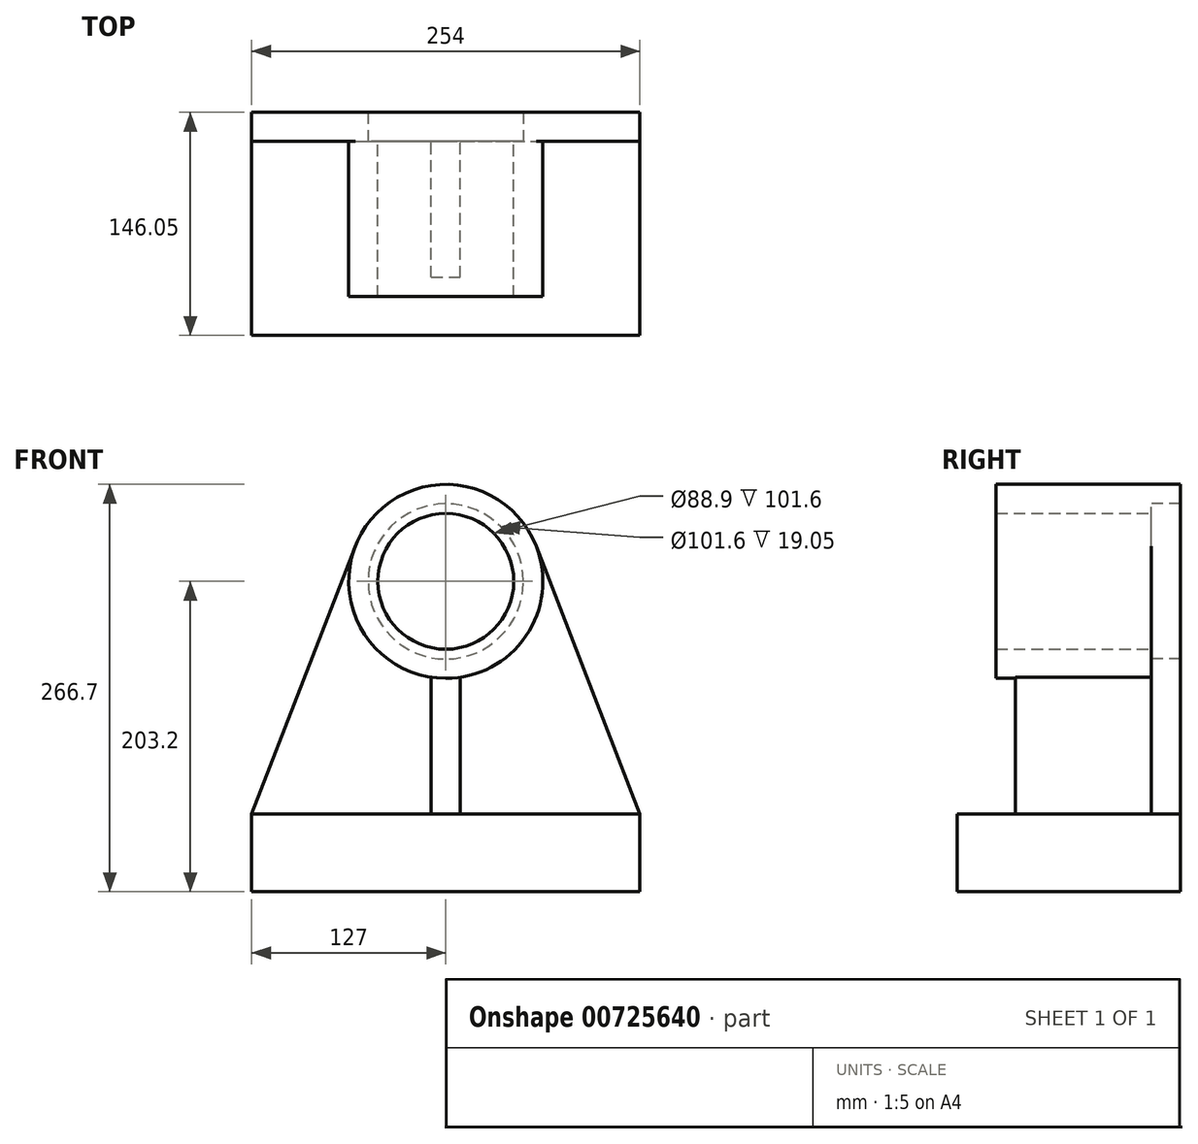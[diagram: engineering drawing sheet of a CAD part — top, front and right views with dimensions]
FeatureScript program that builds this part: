
annotation { "Feature Type Name" : "Feature", "Feature Type Description" : "" }
export const myFeature = defineFeature(function(context is Context, id is Id, definition is map)
    precondition{}
    {
        {
            var Q0;
            Q0=qCreatedBy(makeId("Front.planeOp"),FACE);
            var sketch = newSketch(context, id + "F0", { "sketchPlane" : qUnion([Q0])});
            skLineSegment(sketch, "E0", {"start": v(0, 0) * mm, "end": v(254, 0) * mm});
            skLineSegment(sketch, "E1", {"start": v(254, 0) * mm, "end": v(254, 50.8) * mm});
            skLineSegment(sketch, "E2", {"start": v(254, 50.8) * mm, "end": v(186.23, 226.1) * mm});
            skLineSegment(sketch, "E3", {"start": v(0, 0) * mm, "end": v(0, 50.8) * mm});
            skLineSegment(sketch, "E4", {"start": v(0, 50.8) * mm, "end": v(67.77, 226.1) * mm});
            skArc(sketch, "E5", {"start": v(186.23, 226.1) * mm, "mid": v(127, 266.7) * mm, "end": v(67.77, 226.1) * mm});
            skSolve(sketch);
        }
        {
            var Q0;
            Q0=makeQuery(id+"F0.imprint","IMPRINT",FACE,{"disambiguationData":[TD([[makeQuery(id+"F0.imprint","IMPRINT",EDGE,{"derivedFrom":sQuery(id+"F0.wireOp",EDGE,"E0")}),1.0]])]});
            extrude(context, id + "F1", {"entities" : qUnion([Q0]), "depth" : 19.05 * mm, "offsetDistance" : 25.4 * mm});
        }
        {
            var Q0;
            Q0=makeQuery(id+"F1.opExtrude","CAP_FACE",FACE,{"disambiguationData":[OSD([sQuery(id+"F0.wireOp",EDGE,"E0"),sQuery(id+"F0.wireOp",EDGE,"E1"),sQuery(id+"F0.wireOp",EDGE,"E2"),sQuery(id+"F0.wireOp",EDGE,"E3"),sQuery(id+"F0.wireOp",EDGE,"E4"),sQuery(id+"F0.wireOp",EDGE,"E5")])],"isStart":false});
            var sketch = newSketch(context, id + "F2", { "sketchPlane" : qUnion([Q0])});
            skCircle(sketch, "E6", {"center": v(127, 203.2) * mm, "radius": 44.45 * mm});
            skCircle(sketch, "E7", {"center": v(127, 203.2) * mm, "radius": 63.5 * mm});
            skSolve(sketch);
        }
        {
            var Q0;
            Q0=makeQuery(id+"F2.imprint","IMPRINT",FACE,{"disambiguationData":[TD([[makeQuery(id+"F2.imprint","IMPRINT",EDGE,{"derivedFrom":sQuery(id+"F2.wireOp",EDGE,"E6")}),-1.0]])]});
            extrude(context, id + "F3", {"entities" : qUnion([Q0]), "operationType" : NewBodyOperationType.ADD, "depth" : 101.6 * mm, "offsetDistance" : 25.4 * mm});
        }
        {
            var Q0;
            {var subQ0=sQuery(id+"F0.wireOp",EDGE,"E2");var subQ1=sQuery(id+"F0.wireOp",EDGE,"E1");var subQ2=sQuery(id+"F0.wireOp",EDGE,"E3");var subQ3=sQuery(id+"F0.wireOp",EDGE,"E0");var subQ4=sQuery(id+"F0.wireOp",EDGE,"E4");var subQ5=sQuery(id+"F0.wireOp",EDGE,"E5");Q0=makeQuery(id+"F3.boolean.opBoolean","SPLIT",FACE,{"disambiguationData":[TD([makeQuery(id+"F1.opExtrude","SWEPT_FACE",FACE,{"disambiguationData":[OSD([subQ3])]})])],"derivedFrom":makeQuery(id+"F1.opExtrude","CAP_FACE",FACE,{"disambiguationData":[OSD([subQ3,subQ1,subQ0,subQ2,subQ4,subQ5])],"isStart":false})});}
            var sketch = newSketch(context, id + "F4", { "sketchPlane" : qUnion([Q0])});
            skLineSegment(sketch, "E8.bottom", {"start": v(0, 0) * mm, "end": v(254, 0) * mm});
            skLineSegment(sketch, "E8.top", {"start": v(0, 50.8) * mm, "end": v(254, 50.8) * mm});
            skLineSegment(sketch, "E8.left", {"start": v(0, 0) * mm, "end": v(0, 50.8) * mm});
            skLineSegment(sketch, "E8.right", {"start": v(254, 0) * mm, "end": v(254, 50.8) * mm});
            skSolve(sketch);
        }
        {
            var Q0;
            Q0 = qSketchRegion(id + "F4", true);
            extrude(context, id + "F5", {"entities" : qUnion([Q0]), "operationType" : NewBodyOperationType.ADD, "depth" : 127 * mm, "offsetDistance" : 25.4 * mm});
        }
        {
            var Q0;
            {var subQ0=sQuery(id+"F0.wireOp",EDGE,"E2");var subQ1=sQuery(id+"F0.wireOp",EDGE,"E1");var subQ2=sQuery(id+"F0.wireOp",EDGE,"E3");var subQ3=sQuery(id+"F0.wireOp",EDGE,"E0");var subQ4=sQuery(id+"F0.wireOp",EDGE,"E4");var subQ5=sQuery(id+"F0.wireOp",EDGE,"E5");Q0=makeQuery(id+"F3.boolean.opBoolean","SPLIT",FACE,{"disambiguationData":[TD([makeQuery(id+"F1.opExtrude","SWEPT_FACE",FACE,{"disambiguationData":[OSD([subQ3])]})])],"derivedFrom":makeQuery(id+"F1.opExtrude","CAP_FACE",FACE,{"disambiguationData":[OSD([subQ3,subQ1,subQ0,subQ2,subQ4,subQ5])],"isStart":false})});}
            var sketch = newSketch(context, id + "F6", { "sketchPlane" : qUnion([Q0])});
            skLineSegment(sketch, "E9", {"start": v(117.48, 50.8) * mm, "end": v(136.53, 50.8) * mm});
            skLineSegment(sketch, "E10", {"start": v(136.53, 50.8) * mm, "end": v(136.53, 140.42) * mm});
            skLineSegment(sketch, "E11", {"start": v(117.48, 50.8) * mm, "end": v(117.48, 140.42) * mm});
            skArc(sketch, "E12", {"start": v(117.48, 140.42) * mm, "mid": v(127, 139.82) * mm, "end": v(136.53, 140.42) * mm});
            skSolve(sketch);
        }
        {
            var Q0;
            Q0 = qSketchRegion(id + "F6", true);
            extrude(context, id + "F7", {"entities" : qUnion([Q0]), "operationType" : NewBodyOperationType.ADD, "depth" : 88.9 * mm, "offsetDistance" : 25.4 * mm});
        }
        {
            var Q0;
            Q0=makeQuery(id+"F3.boolean.opBoolean","SPLIT",FACE,{"disambiguationData":[TD([makeQuery(id+"F3.opExtrude","SWEPT_FACE",FACE,{"disambiguationData":[OSD([sQuery(id+"F2.wireOp",EDGE,"E6")])]})])],"derivedFrom":makeQuery(id+"F1.opExtrude","CAP_FACE",FACE,{"disambiguationData":[OSD([sQuery(id+"F0.wireOp",EDGE,"E0"),sQuery(id+"F0.wireOp",EDGE,"E1"),sQuery(id+"F0.wireOp",EDGE,"E2"),sQuery(id+"F0.wireOp",EDGE,"E3"),sQuery(id+"F0.wireOp",EDGE,"E4"),sQuery(id+"F0.wireOp",EDGE,"E5")])],"isStart":false})});
            var sketch = newSketch(context, id + "F8", { "sketchPlane" : qUnion([Q0])});
            skCircle(sketch, "E13", {"center": v(127, 203.2) * mm, "radius": 50.8 * mm});
            skSolve(sketch);
        }
        {
            var Q0;
            Q0 = qSketchRegion(id + "F8", true);
            extrude(context, id + "F9", {"entities" : qUnion([Q0]), "operationType" : NewBodyOperationType.REMOVE, "endBound" : BoundingType.THROUGH_ALL, "oppositeDirection" : true, "depth" : 25.4 * mm, "offsetDistance" : 25.4 * mm});
        }
    });
